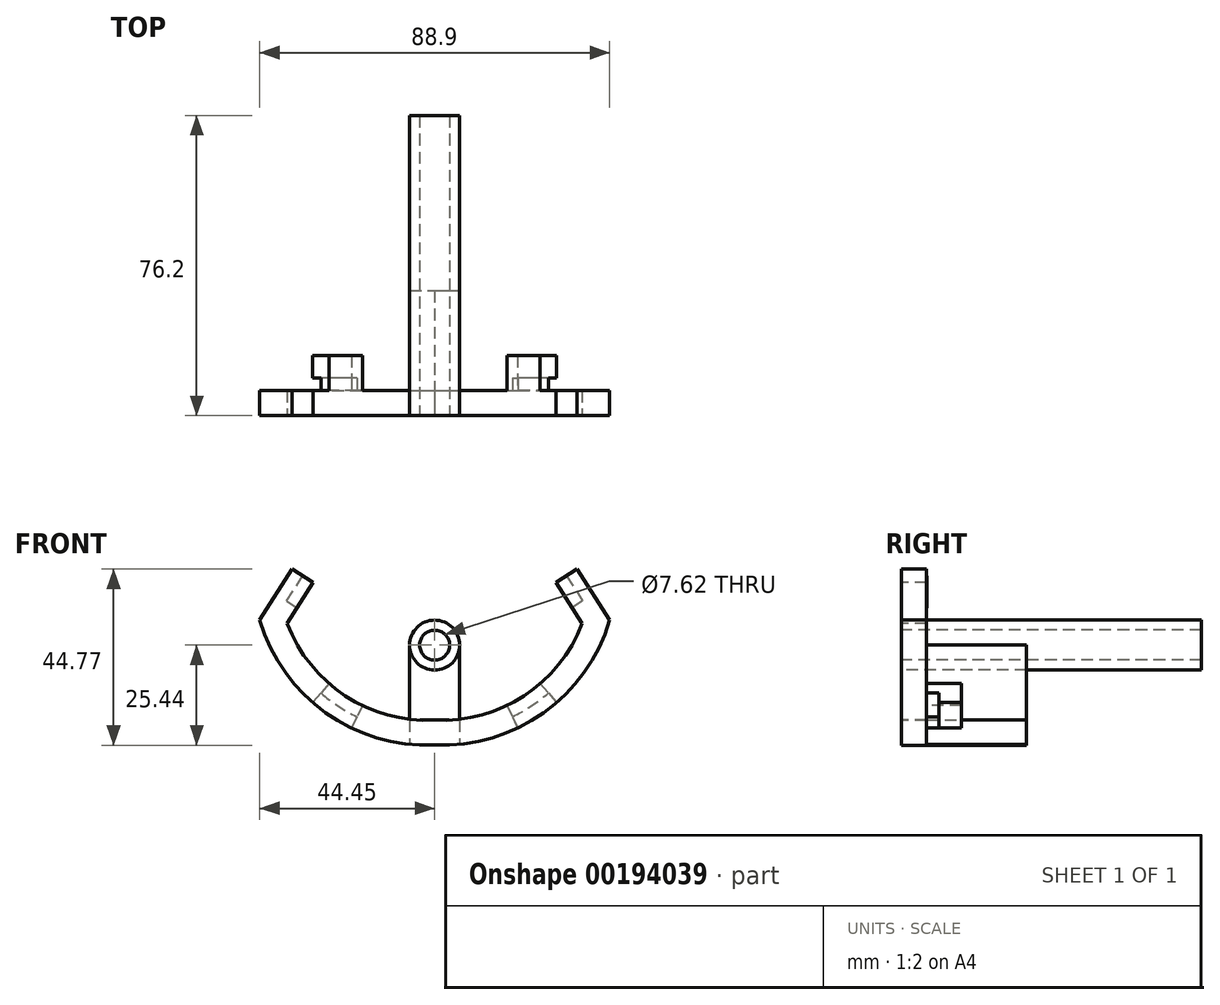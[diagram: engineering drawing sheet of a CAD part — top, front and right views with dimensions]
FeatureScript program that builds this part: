
annotation { "Feature Type Name" : "Feature", "Feature Type Description" : "" }
export const myFeature = defineFeature(function(context is Context, id is Id, definition is map)
    precondition{}
    {
        {
            var Q0;
            Q0=qCreatedBy(makeId("Front.planeOp"),FACE);
            var sketch = newSketch(context, id + "F0", { "sketchPlane" : qUnion([Q0])});
            skCircle(sketch, "E0", {"center": v(0, 25.4) * mm, "radius": 3.81 * mm});
            skCircle(sketch, "E1", {"center": v(0, 25.4) * mm, "radius": 6.35 * mm});
            skSolve(sketch);
        }
        {
            var Q0;
            Q0 = qSketchRegion(id + "F0", true);
            extrude(context, id + "F1", {"entities" : qUnion([Q0]), "oppositeDirection" : true, "depth" : 76.2 * mm});
        }
        {
            var Q0;
            Q0=qCreatedBy(makeId("Front.planeOp"),FACE);
            var sketch = newSketch(context, id + "F2", { "sketchPlane" : qUnion([Q0])});
            skArc(sketch, "E2", {"start": v(-44.45, 31.75) * mm, "mid": v(-27.68, 8.24) * mm, "end": v(0, 0) * mm});
            skArc(sketch, "E3.1", {"start": v(-37.47, 30.9) * mm, "mid": v(-22.72, 12.54) * mm, "end": v(0, 6.36) * mm});
            skLineSegment(sketch, "E4", {"start": v(-44.45, 31.75) * mm, "end": v(-39.6, 39.37) * mm});
            skArc(sketch, "E5.MirrorCS", {"start": v(44.45, 31.75) * mm, "mid": v(27.68, 8.24) * mm, "end": v(0, 0) * mm});
            skArc(sketch, "E6.MirrorCS", {"start": v(37.47, 30.9) * mm, "mid": v(22.72, 12.54) * mm, "end": v(0, 6.36) * mm});
            skLineSegment(sketch, "E7.MirrorCS", {"start": v(44.45, 31.75) * mm, "end": v(39.6, 39.37) * mm});
            skLineSegment(sketch, "E8", {"start": v(-39.6, 39.37) * mm, "end": v(-36.2, 44.73) * mm});
            skLineSegment(sketch, "E9", {"start": v(-36.2, 44.73) * mm, "end": v(-30.84, 41.32) * mm});
            skLineSegment(sketch, "E10", {"start": v(-30.84, 41.32) * mm, "end": v(-37.47, 30.9) * mm});
            skLineSegment(sketch, "E11.MirrorCS", {"start": v(36.2, 44.73) * mm, "end": v(30.84, 41.32) * mm});
            skLineSegment(sketch, "E12.MirrorCS", {"start": v(39.6, 39.37) * mm, "end": v(36.2, 44.73) * mm});
            skLineSegment(sketch, "E13.MirrorCS", {"start": v(30.84, 41.32) * mm, "end": v(37.47, 30.9) * mm});
            skPoint(sketch, "E14.orphan", {"position": v(39.6, 39.37) * mm});
            skSolve(sketch);
        }
        {
            var Q0;
            Q0 = qSketchRegion(id + "F2", true);
            extrude(context, id + "F3", {"entities" : qUnion([Q0]), "oppositeDirection" : true, "depth" : 6.35 * mm});
        }
        {
            var Q0;
            Q0=makeQuery(id+"F3.opExtrude","CAP_FACE",FACE,{"disambiguationData":[OSD([sQuery(id+"F2.wireOp",EDGE,"E2"),sQuery(id+"F2.wireOp",EDGE,"E3.1"),sQuery(id+"F2.wireOp",EDGE,"E4"),sQuery(id+"F2.wireOp",EDGE,"E5.MirrorCS"),sQuery(id+"F2.wireOp",EDGE,"E6.MirrorCS"),sQuery(id+"F2.wireOp",EDGE,"E7.MirrorCS"),sQuery(id+"F2.wireOp",EDGE,"E8"),sQuery(id+"F2.wireOp",EDGE,"E9"),sQuery(id+"F2.wireOp",EDGE,"E10"),sQuery(id+"F2.wireOp",EDGE,"E11.MirrorCS"),sQuery(id+"F2.wireOp",EDGE,"E12.MirrorCS"),sQuery(id+"F2.wireOp",EDGE,"E13.MirrorCS")])],"isStart":false});
            cPlane(context, id + "F4", {"entities" : qUnion([Q0]), "cplaneType" : CPlaneType.OFFSET, "offset" : 0 * mm, "width" : 152.4 * mm, "height" : 152.4 * mm});
        }
        {
            var Q0;
            Q0=qCreatedBy(id+"F4.planeOp",FACE);
            var sketch = newSketch(context, id + "F5", { "sketchPlane" : qUnion([Q0])});
            skPoint(sketch, "E15", {"position": v(-30.84, 41.32) * mm});
            skLineSegment(sketch, "E16", {"start": v(-30.84, 41.32) * mm, "end": v(-37.47, 30.9) * mm});
            skLineSegment(sketch, "E17", {"start": v(-30.84, 41.32) * mm, "end": v(-36.2, 44.73) * mm});
            skLineSegment(sketch, "E18", {"start": v(-36.2, 44.73) * mm, "end": v(-40.29, 38.3) * mm});
            skLineSegment(sketch, "E19", {"start": v(-40.29, 38.3) * mm, "end": v(-34.93, 34.9) * mm});
            skPoint(sketch, "E20.MirrorP", {"position": v(30.84, 41.32) * mm});
            skLineSegment(sketch, "E21.MirrorCS", {"start": v(40.29, 38.3) * mm, "end": v(34.93, 34.9) * mm});
            skLineSegment(sketch, "E22.MirrorCS", {"start": v(36.2, 44.73) * mm, "end": v(40.29, 38.3) * mm});
            skLineSegment(sketch, "E23.MirrorCS", {"start": v(30.84, 41.32) * mm, "end": v(37.47, 30.9) * mm});
            skLineSegment(sketch, "E24.MirrorCS", {"start": v(30.84, 41.32) * mm, "end": v(36.2, 44.73) * mm});
            skSolve(sketch);
        }
        {
            var Q0;
            Q0 = qSketchRegion(id + "F5", true);
            extrude(context, id + "F6", {"entities" : qUnion([Q0]), "depth" : 3 / 203.2 * mm});
        }
        {
            var Q0;
            Q0=makeQuery(id+"F6.opExtrude","SWEPT_FACE",FACE,{"disambiguationData":[OSD([sQuery(id+"F5.wireOp",EDGE,"E18")])]});
            cPlane(context, id + "F7", {"entities" : qUnion([Q0]), "cplaneType" : CPlaneType.OFFSET, "offset" : 0 * mm, "width" : 152.4 * mm, "height" : 152.4 * mm});
        }
        {
            var Q0;
            Q0=qCreatedBy(id+"F7.planeOp",FACE);
            var sketch = newSketch(context, id + "F8", { "sketchPlane" : qUnion([Q0])});
            skLineSegment(sketch, "E25.bottom", {"start": v(6.35, 18.33) * mm, "end": v(9.53, 18.33) * mm});
            skLineSegment(sketch, "E25.top", {"start": v(6.35, 10.7) * mm, "end": v(9.53, 10.7) * mm});
            skLineSegment(sketch, "E25.left", {"start": v(6.35, 18.33) * mm, "end": v(6.35, 10.7) * mm});
            skLineSegment(sketch, "E25.right", {"start": v(9.53, 18.33) * mm, "end": v(9.53, 10.7) * mm});
            skSolve(sketch);
        }
        {
            var Q0;
            Q0 = qSketchRegion(id + "F8", true);
            extrude(context, id + "F9", {"entities" : qUnion([Q0]), "operationType" : NewBodyOperationType.REMOVE, "oppositeDirection" : true, "depth" : 3.17 * mm});
        }
        {
            var Q0;
            Q0=makeQuery(id+"F6.opExtrude","SWEPT_FACE",FACE,{"disambiguationData":[OSD([sQuery(id+"F5.wireOp",EDGE,"E22.MirrorCS")])]});
            var sketch = newSketch(context, id + "F10", { "sketchPlane" : qUnion([Q0])});
            skLineSegment(sketch, "E26.bottom", {"start": v(-6.35, 18.33) * mm, "end": v(-9.53, 18.33) * mm});
            skLineSegment(sketch, "E26.top", {"start": v(-6.35, 10.7) * mm, "end": v(-9.52, 10.7) * mm});
            skLineSegment(sketch, "E26.left", {"start": v(-6.35, 18.33) * mm, "end": v(-6.35, 10.7) * mm});
            skLineSegment(sketch, "E26.right", {"start": v(-9.53, 18.33) * mm, "end": v(-9.52, 10.7) * mm});
            skSolve(sketch);
        }
        {
            var Q0;
            Q0 = qSketchRegion(id + "F10", true);
            extrude(context, id + "F11", {"entities" : qUnion([Q0]), "operationType" : NewBodyOperationType.REMOVE, "oppositeDirection" : true, "depth" : 3.17 * mm});
        }
        {
            var Q0;
            Q0=makeQuery(id+"F3.opExtrude","CAP_FACE",FACE,{"disambiguationData":[OSD([sQuery(id+"F2.wireOp",EDGE,"E2"),sQuery(id+"F2.wireOp",EDGE,"E3.1"),sQuery(id+"F2.wireOp",EDGE,"E4"),sQuery(id+"F2.wireOp",EDGE,"E5.MirrorCS"),sQuery(id+"F2.wireOp",EDGE,"E6.MirrorCS"),sQuery(id+"F2.wireOp",EDGE,"E7.MirrorCS"),sQuery(id+"F2.wireOp",EDGE,"E8"),sQuery(id+"F2.wireOp",EDGE,"E9"),sQuery(id+"F2.wireOp",EDGE,"E10"),sQuery(id+"F2.wireOp",EDGE,"E11.MirrorCS"),sQuery(id+"F2.wireOp",EDGE,"E12.MirrorCS"),sQuery(id+"F2.wireOp",EDGE,"E13.MirrorCS")])],"isStart":false});
            var sketch = newSketch(context, id + "F12", { "sketchPlane" : qUnion([Q0])});
            skArc(sketch, "E27.0", {"start": v(-44.45, 31.75) * mm, "mid": v(-27.68, 8.24) * mm, "end": v(0, 0) * mm});
            skArc(sketch, "E28.0", {"start": v(44.45, 31.75) * mm, "mid": v(27.68, 8.24) * mm, "end": v(0, 0) * mm});
            skArc(sketch, "E29.0", {"start": v(-38.36, 33.56) * mm, "mid": v(-23.99, 13.4) * mm, "end": v(-0.26, 6.34) * mm});
            skArc(sketch, "E30.0", {"start": v(38.36, 33.56) * mm, "mid": v(23.99, 13.4) * mm, "end": v(0.26, 6.34) * mm});
            skLineSegment(sketch, "E31", {"start": v(-0.26, 6.34) * mm, "end": v(0.26, 6.34) * mm});
            skLineSegment(sketch, "E32", {"start": v(0, 6.36) * mm, "end": v(-12.22, 6.36) * mm, "construction": true});
            skPoint(sketch, "E33", {"position": v(-6.35, 6.36) * mm});
            skLineSegment(sketch, "E34", {"start": v(-6.35, 6.36) * mm, "end": v(-6.35, 0.2) * mm});
            skLineSegment(sketch, "E35.MirrorCS", {"start": v(6.35, 6.36) * mm, "end": v(6.35, 0.2) * mm});
            skLineSegment(sketch, "E36", {"start": v(6.35, 6.36) * mm, "end": v(-6.35, 6.36) * mm});
            skPoint(sketch, "E37.MirrorCS.end.orphan", {"position": v(6.35, 6.58) * mm});
            skPoint(sketch, "E38.end.orphan", {"position": v(-6.35, 6.58) * mm});
            skSolve(sketch);
        }
        {
            var Q0;
            Q0 = qSketchRegion(id + "F12", true);
            extrude(context, id + "F13", {"entities" : qUnion([Q0]), "operationType" : NewBodyOperationType.ADD, "depth" : 25.4 * mm});
        }
        {
            var Q0;
            Q0=qCreatedBy(makeId("Top.planeOp"),FACE);
            cPlane(context, id + "F14", {"entities" : qUnion([Q0]), "cplaneType" : CPlaneType.OFFSET, "offset" : 7.62 * mm, "width" : 152.4 * mm, "height" : 152.4 * mm});
        }
        {
            var Q0;
            Q0=qCreatedBy(id+"F14.planeOp",FACE);
            var sketch = newSketch(context, id + "F15", { "sketchPlane" : qUnion([Q0])});
            skLineSegment(sketch, "E39.bottom", {"start": v(6.35, 31.75) * mm, "end": v(-6.35, 31.75) * mm});
            skLineSegment(sketch, "E39.top", {"start": v(6.35, 6.35) * mm, "end": v(-6.35, 6.35) * mm});
            skLineSegment(sketch, "E39.left", {"start": v(6.35, 31.75) * mm, "end": v(6.35, 6.35) * mm});
            skLineSegment(sketch, "E39.right", {"start": v(-6.35, 31.75) * mm, "end": v(-6.35, 6.35) * mm});
            skPoint(sketch, "E39.middle", {"position": v(0, 19.05) * mm});
            skSolve(sketch);
        }
        {
            var Q0;
            Q0 = qSketchRegion(id + "F15", true);
            var Q1;
            Q1=makeQuery(id+"F1.opExtrude","SWEPT_BODY",BODY,{"disambiguationData":[OSD([sQuery(id+"F0.wireOp",EDGE,"E0"),sQuery(id+"F0.wireOp",EDGE,"E1")])]});
            var Q2;
            Q2=makeQuery(id+"F13.opExtrude","SWEPT_FACE",FACE,{"disambiguationData":[OSD([sQuery(id+"F12.wireOp",EDGE,"E36")])]});
            extrude(context, id + "F16", {"entities" : qUnion([Q0]), "endBound" : BoundingType.UP_TO_BODY, "endBoundEntityBody" : qUnion([Q1]), "depth" : 25.4 * mm, "hasSecondDirection" : true, "secondDirectionBound" : SecondDirectionBoundingType.UP_TO_SURFACE, "secondDirectionOppositeDirection" : true, "secondDirectionBoundEntityFace" : qUnion([Q2]), "secondDirectionDepth" : 25.4 * mm});
        }
        {
            var Q0;
            {var subQ0=sQuery(id+"F2.wireOp",EDGE,"E11.MirrorCS");var subQ1=sQuery(id+"F2.wireOp",EDGE,"E12.MirrorCS");var subQ2=sQuery(id+"F2.wireOp",EDGE,"E7.MirrorCS");var subQ3=sQuery(id+"F2.wireOp",EDGE,"E6.MirrorCS");var subQ4=sQuery(id+"F2.wireOp",EDGE,"E5.MirrorCS");var subQ5=sQuery(id+"F2.wireOp",EDGE,"E13.MirrorCS");Q0=makeQuery(id+"F13.boolean.opBoolean","SPLIT",FACE,{"disambiguationData":[TD([makeQuery(id+"F3.opExtrude","SWEPT_FACE",FACE,{"disambiguationData":[OSD([subQ4])]})])],"derivedFrom":makeQuery(id+"F3.opExtrude","CAP_FACE",FACE,{"disambiguationData":[OSD([sQuery(id+"F2.wireOp",EDGE,"E2"),sQuery(id+"F2.wireOp",EDGE,"E3.1"),sQuery(id+"F2.wireOp",EDGE,"E4"),subQ4,subQ3,subQ2,sQuery(id+"F2.wireOp",EDGE,"E8"),sQuery(id+"F2.wireOp",EDGE,"E9"),sQuery(id+"F2.wireOp",EDGE,"E10"),subQ0,subQ1,subQ5])],"isStart":false})});}
            var sketch = newSketch(context, id + "F17", { "sketchPlane" : qUnion([Q0])});
            skPoint(sketch, "E40", {"position": v(0, 25.4) * mm});
            skPoint(sketch, "E41", {"position": v(-40.32, 38.24) * mm});
            skLineSegment(sketch, "E42", {"start": v(-40.32, 38.24) * mm, "end": v(-40.32, 0) * mm, "construction": true});
            skPoint(sketch, "E43", {"position": v(-40.32, 25.4) * mm});
            skPoint(sketch, "E44", {"position": v(-40.32, 12.56) * mm});
            skLineSegment(sketch, "E45", {"start": v(-40.32, 12.56) * mm, "end": v(-22.75, 12.56) * mm, "construction": true});
            skArc(sketch, "E46.0", {"start": v(-44.45, 31.75) * mm, "mid": v(-30.2, 10.18) * mm, "end": v(-6.35, 0.2) * mm});
            skArc(sketch, "E47.0", {"start": v(-37.47, 30.9) * mm, "mid": v(-24.24, 13.59) * mm, "end": v(-3.68, 6.36) * mm});
            skPoint(sketch, "E48", {"position": v(-26.8, 15.63) * mm});
            skPoint(sketch, "E49", {"position": v(-18.33, 10.06) * mm});
            skLineSegment(sketch, "E50", {"start": v(-26.8, 15.63) * mm, "end": v(-30.96, 10.83) * mm});
            skLineSegment(sketch, "E51", {"start": v(-18.33, 10.06) * mm, "end": v(-21.07, 4.34) * mm});
            skArc(sketch, "E52.0", {"start": v(-41.4, 32.65) * mm, "mid": v(-40.9, 31.06) * mm, "end": v(-40.32, 29.49) * mm});
            skArc(sketch, "E53.trimOffspring", {"start": v(-28.88, 13.23) * mm, "mid": v(-24.5, 9.9) * mm, "end": v(-19.7, 7.2) * mm});
            skLineSegment(sketch, "E54.MirrorCS", {"start": v(18.33, 10.06) * mm, "end": v(21.07, 4.34) * mm});
            skArc(sketch, "E55.MirrorCS", {"start": v(44.45, 31.75) * mm, "mid": v(30.2, 10.18) * mm, "end": v(6.35, 0.2) * mm});
            skArc(sketch, "E56.MirrorCS", {"start": v(37.47, 30.9) * mm, "mid": v(24.24, 13.59) * mm, "end": v(3.68, 6.36) * mm});
            skLineSegment(sketch, "E57.MirrorCS", {"start": v(26.8, 15.63) * mm, "end": v(30.96, 10.83) * mm});
            skArc(sketch, "E58.MirrorCS", {"start": v(28.88, 13.23) * mm, "mid": v(24.5, 9.9) * mm, "end": v(19.7, 7.2) * mm});
            skSolve(sketch);
        }
        {
            var Q0;
            Q0 = qSketchRegion(id + "F17", true);
            extrude(context, id + "F18", {"entities" : qUnion([Q0]), "operationType" : NewBodyOperationType.ADD, "depth" : 8.9 * mm});
        }
        {
            var Q0;
            {var subQ1=sQuery(id+"F12.wireOp",EDGE,"E34");var subQ10=makeQuery(id+"F13.opExtrude","CAP_EDGE",EDGE,{"disambiguationData":[OSD([subQ1])],"isStart":true});Q0=makeQuery(id+"F17.imprint","IMPRINT",FACE,{"disambiguationData":[TD([[makeQuery(id+"F17.imprint","IMPRINT",EDGE,{"derivedFrom":subQ10}),-1.0]])]});}
            var sketch = newSketch(context, id + "F19", { "sketchPlane" : qUnion([Q0])});
            skPoint(sketch, "E59", {"position": v(-18.33, 10.06) * mm});
            skPoint(sketch, "E60", {"position": v(-26.8, 15.63) * mm});
            skArc(sketch, "E61.0", {"start": v(-44.45, 31.75) * mm, "mid": v(-30.2, 10.18) * mm, "end": v(-6.35, 0.2) * mm});
            skArc(sketch, "E62.0", {"start": v(-37.47, 30.9) * mm, "mid": v(-24.24, 13.59) * mm, "end": v(-3.68, 6.36) * mm});
            skLineSegment(sketch, "E63", {"start": v(-26.8, 15.63) * mm, "end": v(-30.96, 10.83) * mm});
            skLineSegment(sketch, "E64", {"start": v(-18.33, 10.06) * mm, "end": v(-21.13, 4.37) * mm});
            skArc(sketch, "E65.0", {"start": v(-41.4, 32.65) * mm, "mid": v(-28.17, 12.63) * mm, "end": v(-6.03, 3.35) * mm});
            skLineSegment(sketch, "E66.MirrorCS", {"start": v(18.33, 10.06) * mm, "end": v(21.13, 4.37) * mm});
            skArc(sketch, "E67.MirrorCS", {"start": v(44.45, 31.75) * mm, "mid": v(30.2, 10.18) * mm, "end": v(6.35, 0.2) * mm});
            skArc(sketch, "E68.MirrorCS", {"start": v(41.4, 32.65) * mm, "mid": v(28.17, 12.63) * mm, "end": v(6.03, 3.35) * mm});
            skLineSegment(sketch, "E69.MirrorCS", {"start": v(26.8, 15.63) * mm, "end": v(30.96, 10.83) * mm});
            skArc(sketch, "E70.MirrorCS", {"start": v(37.47, 30.9) * mm, "mid": v(24.24, 13.59) * mm, "end": v(3.68, 6.36) * mm});
            skSolve(sketch);
        }
        {
            var Q0;
            Q0 = qSketchRegion(id + "F19", true);
            extrude(context, id + "F20", {"entities" : qUnion([Q0]), "operationType" : NewBodyOperationType.REMOVE, "depth" : 3.17 * mm});
        }
    });
